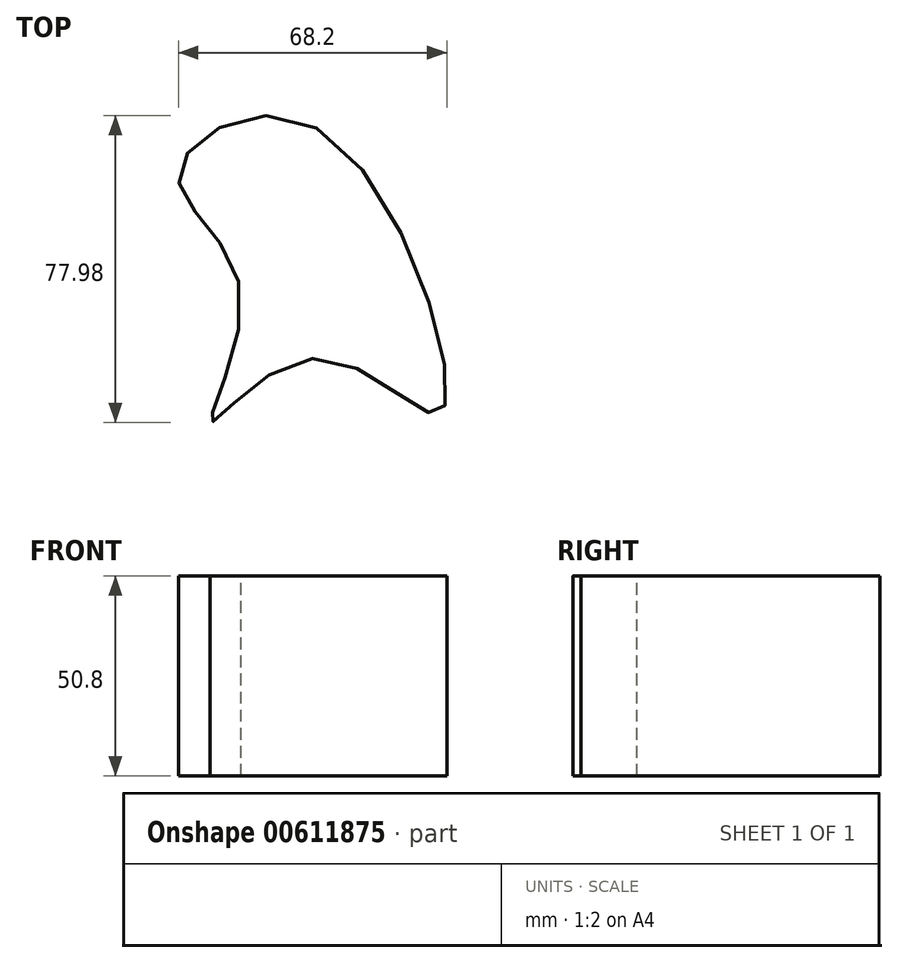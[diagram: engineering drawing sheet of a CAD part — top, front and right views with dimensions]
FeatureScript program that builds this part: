
annotation { "Feature Type Name" : "Feature", "Feature Type Description" : "" }
export const myFeature = defineFeature(function(context is Context, id is Id, definition is map)
    precondition{}
    {
        {
            var Q0;
            Q0=qCreatedBy(makeId("Top.planeOp"),FACE);
            var sketch = newSketch(context, id + "F0", { "sketchPlane" : qUnion([Q0])});
            skFitSpline(sketch, "E0", {"points": [v(0, 40.57) * mm, v(-35.01, 29.09) * mm, v(-19.45, 0) * mm, v(-26.86, -34.27) * mm, v(0, -17.97) * mm, v(31.68, -31.68) * mm, v(0, 40.57) * mm]});
            skSolve(sketch);
        }
        {
            var Q0;
            Q0=makeQuery(id+"F0.imprint","IMPRINT",FACE,{"disambiguationData":[TD([[makeQuery(id+"F0.imprint","IMPRINT",EDGE,{"derivedFrom":sQuery(id+"F0.wireOp",EDGE,"E0")}),1.0]])]});
            extrude(context, id + "F1", {"entities" : qUnion([Q0]), "depth" : 25.4 * mm, "offsetDistance" : 25.4 * mm});
        }
        {
            var Q0;
            Q0=makeQuery(id+"F1.opExtrude","CAP_FACE",FACE,{"disambiguationData":[OSD([sQuery(id+"F0.wireOp",EDGE,"E0")])],"isStart":false});
            extrude(context, id + "F2", {"entities" : qUnion([Q0]), "operationType" : NewBodyOperationType.ADD, "depth" : 25.4 * mm, "offsetDistance" : 25.4 * mm});
        }
    });
